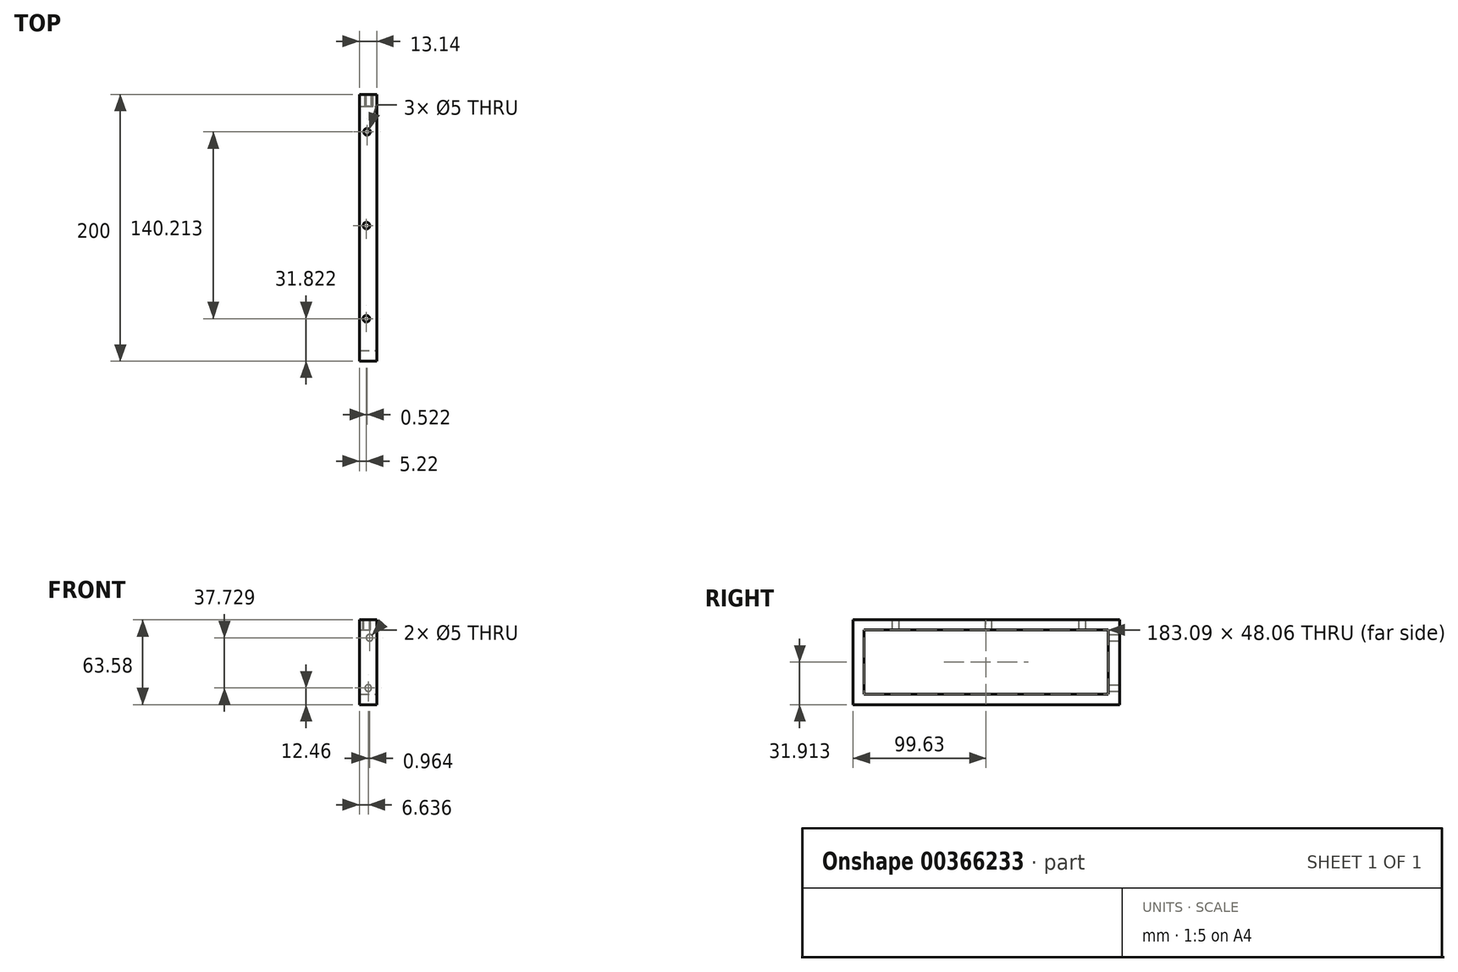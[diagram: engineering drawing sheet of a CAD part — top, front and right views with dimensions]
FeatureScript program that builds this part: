
annotation { "Feature Type Name" : "Feature", "Feature Type Description" : "" }
export const myFeature = defineFeature(function(context is Context, id is Id, definition is map)
    precondition{}
    {
        {
            var Q0;
            Q0=qCreatedBy(makeId("Front.planeOp"),FACE);
            var sketch = newSketch(context, id + "F0", { "sketchPlane" : qUnion([Q0])});
            skLineSegment(sketch, "E0.bottom", {"start": v(-68.3, 25.52) * mm, "end": v(-55.16, 25.52) * mm});
            skLineSegment(sketch, "E0.top", {"start": v(-68.3, -38.06) * mm, "end": v(-55.16, -38.06) * mm});
            skLineSegment(sketch, "E0.left", {"start": v(-68.3, 25.52) * mm, "end": v(-68.3, -38.06) * mm});
            skLineSegment(sketch, "E0.right", {"start": v(-55.16, 25.52) * mm, "end": v(-55.16, -38.06) * mm});
            skSolve(sketch);
        }
        {
            var Q0;
            Q0=makeQuery(id+"F0.imprint","IMPRINT",FACE,{"disambiguationData":[TD([[makeQuery(id+"F0.imprint","IMPRINT",EDGE,{"derivedFrom":sQuery(id+"F0.wireOp",EDGE,"E0.bottom")}),-1.0]])]});
            extrude(context, id + "F1", {"entities" : qUnion([Q0]), "depth" : 200 * mm});
        }
        {
            var Q0;
            Q0=makeQuery(id+"F1.opExtrude","SWEPT_FACE",FACE,{"disambiguationData":[OSD([sQuery(id+"F0.wireOp",EDGE,"E0.bottom")])]});
            var sketch = newSketch(context, id + "F2", { "sketchPlane" : qUnion([Q0])});
            skPoint(sketch, "E1", {"position": v(-63.08, -168.18) * mm});
            skPoint(sketch, "E2", {"position": v(-62.98, -98.36) * mm});
            skPoint(sketch, "E3", {"position": v(-62.56, -27.97) * mm});
            skSolve(sketch);
        }
        {
            var Q0;
            Q0=sQuery(id+"F2.wireOp",VERTEX,"E1");
            var Q1;
            Q1=sQuery(id+"F2.wireOp",VERTEX,"E2");
            var Q2;
            Q2=sQuery(id+"F2.wireOp",VERTEX,"E3");
            var Q3;
            Q3=makeQuery(id+"F1.opExtrude","SWEPT_BODY",BODY,{"disambiguationData":[OSD([sQuery(id+"F0.wireOp",EDGE,"E0.bottom"),sQuery(id+"F0.wireOp",EDGE,"E0.top"),sQuery(id+"F0.wireOp",EDGE,"E0.left"),sQuery(id+"F0.wireOp",EDGE,"E0.right")])]});
            hole(context, id + "F3", {"style" : HoleStyle.SIMPLE, "endStyle" : HoleEndStyle.BLIND, "holeDiameter" : 5 * mm, "holeDepth" : 12 * mm, "isTappedThrough" : true, "tappedDepth" : 12 * mm, "tapClearance" : 3, "locations" : qUnion([Q0, Q1, Q2]), "scope" : qUnion([Q3])});
        }
        {
            var Q0;
            Q0=makeQuery(id+"F0.imprint","IMPRINT",FACE,{"disambiguationData":[TD([[makeQuery(id+"F0.imprint","IMPRINT",EDGE,{"derivedFrom":sQuery(id+"F0.wireOp",EDGE,"E0.bottom")}),-1.0]])]});
            var sketch = newSketch(context, id + "F4", { "sketchPlane" : qUnion([Q0])});
            skPoint(sketch, "E4", {"position": v(-60.7, 12.13) * mm});
            skPoint(sketch, "E5", {"position": v(-61.66, -25.6) * mm});
            skSolve(sketch);
        }
        {
            var Q0;
            Q0=sQuery(id+"F4.wireOp",VERTEX,"E4");
            var Q1;
            Q1=sQuery(id+"F4.wireOp",VERTEX,"E5");
            var Q2;
            Q2=makeQuery(id+"F1.opExtrude","SWEPT_BODY",BODY,{"disambiguationData":[OSD([sQuery(id+"F0.wireOp",EDGE,"E0.bottom"),sQuery(id+"F0.wireOp",EDGE,"E0.top"),sQuery(id+"F0.wireOp",EDGE,"E0.left"),sQuery(id+"F0.wireOp",EDGE,"E0.right")])]});
            hole(context, id + "F5", {"style" : HoleStyle.SIMPLE, "endStyle" : HoleEndStyle.BLIND, "oppositeDirection" : true, "holeDiameter" : 5 * mm, "holeDepth" : 12 * mm, "isTappedThrough" : true, "tappedDepth" : 12 * mm, "tapClearance" : 3, "locations" : qUnion([Q0, Q1]), "scope" : qUnion([Q2])});
        }
        {
            var Q0;
            Q0=makeQuery(id+"F1.opExtrude","SWEPT_FACE",FACE,{"disambiguationData":[OSD([sQuery(id+"F0.wireOp",EDGE,"E0.right")])]});
            var sketch = newSketch(context, id + "F6", { "sketchPlane" : qUnion([Q0])});
            skLineSegment(sketch, "E6.bottom", {"start": v(-191.92, 17.89) * mm, "end": v(-8.82, 17.89) * mm});
            skLineSegment(sketch, "E6.top", {"start": v(-191.92, -30.18) * mm, "end": v(-8.82, -30.18) * mm});
            skLineSegment(sketch, "E6.left", {"start": v(-191.92, 17.89) * mm, "end": v(-191.92, -30.18) * mm});
            skLineSegment(sketch, "E6.right", {"start": v(-8.82, 17.89) * mm, "end": v(-8.82, -30.18) * mm});
            skSolve(sketch);
        }
        {
            var Q0;
            Q0=qSketchRegion(id+"F6",true);
            extrude(context, id + "F7", {"entities" : qUnion([Q0]), "operationType" : NewBodyOperationType.REMOVE, "oppositeDirection" : true, "depth" : 25 * mm});
        }
    });
